# Revit family: P200921MX-061c_MSC21C6MFZ
name_source: partatom
category: Specialty Equipment
units: mm (PartAtom-declared; Revit-internal decimal feet)

## family parameters
Always vertical = No
Cut with Voids When Loaded = No
Enable Cutting in Views = No
Maintain Annotation Orientation = No
Part Type = Normal
Room Calculation Point = No
Round Connector Dimension = Use Diameter
Shared = No
Work Plane-Based = No

## types (1)
- MSC21C6MFZ
    Accent Material = ARCAT - Plastic - Gray
    Amps = 0 A
    Body Material = ARCAT - Metal - Steel - Gray
    Clearance Material = ARCAT - Clearance
    Default Elevation = 0"
    Depth = 29 3/4"
    Description = 36- Inch Wide Counter Depth Side-by-Side Refrigerator- 21 Cu. Ft.
    Dimension Guide = http://access.whirlpool.com Guide&sku=MSC21C6MFZ&language=EN
    Display Panel Material = ARCAT - Glass - Tempered - Black
    Door Material = ARCAT - Metal - Steel - Stainless
    Energy Guide = http://access.whirlpool.com Guide&sku=MSC21C6MFZ&language=EN
    Family Name = Refrigeration
    Feature 1 = Fingerprint Resistant Stainless Steel
    Feature 2 = PowerCold® Feature
    Feature 3 = Store-N-Door® Ice Dispensing System
    Glass Material = ARCAT - Glass - Tempered - Black
    Handle Material = ARCAT - Metal - Steel -Gray Light
    Height = 69"
    Installation-Fabrication = http://access.whirlpool.com Instruction&sku=MSC21C6MFZ&language=EN
    Manufacturer = Maytag
    Model = MSC21C6MFZ
    Voltage = 0 V
    Width = 36"

## geometry (parser evidence)
native form markers: Sweep x3
no freeform markers — native parametric forms only
